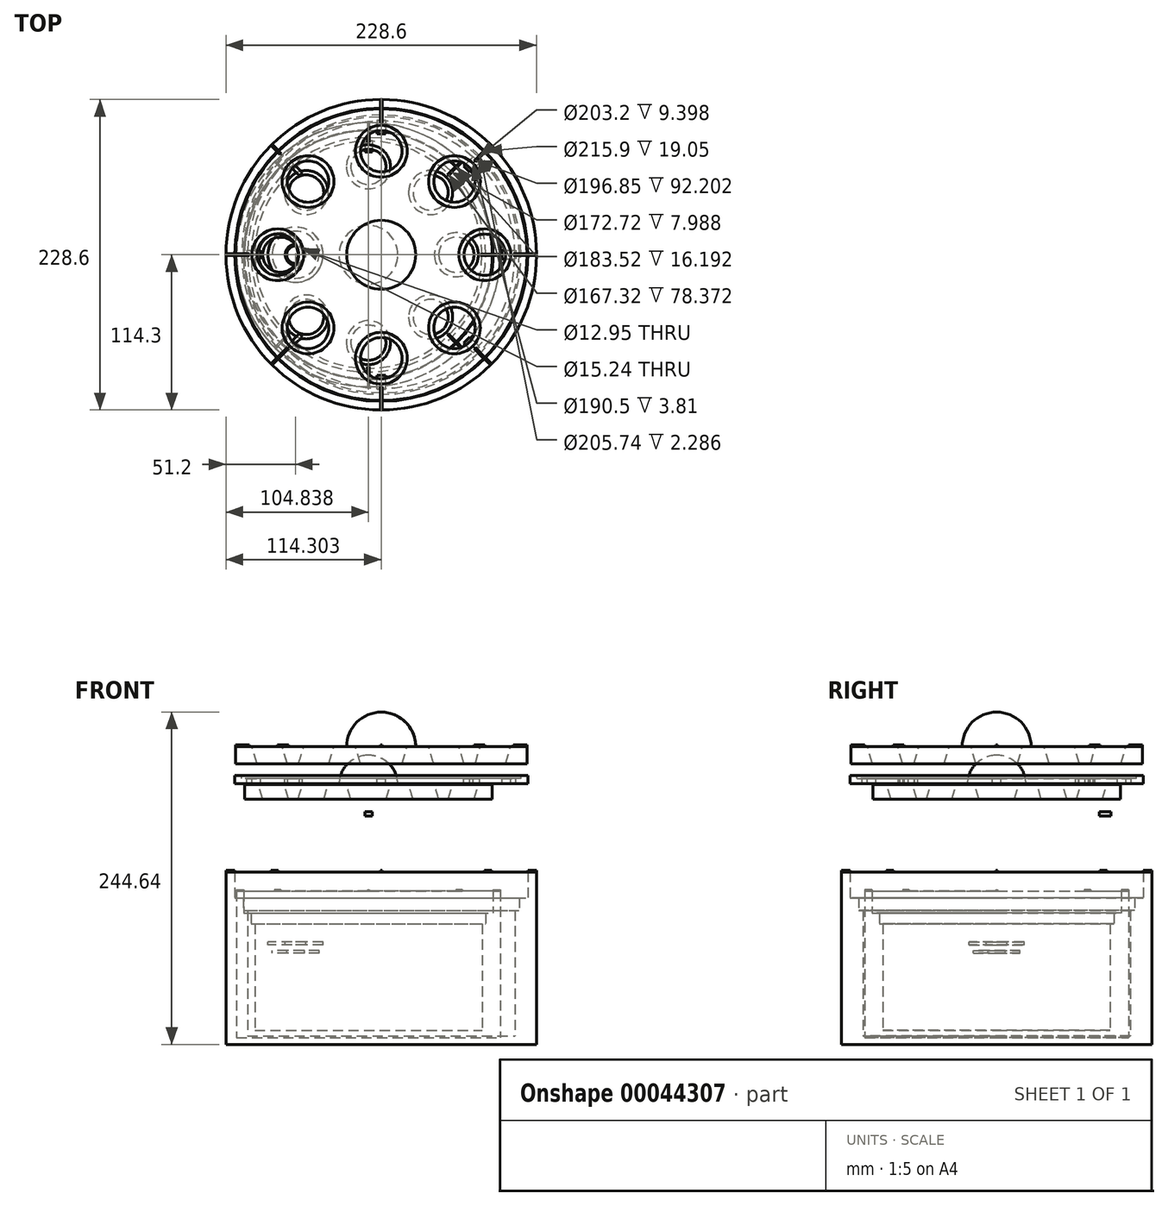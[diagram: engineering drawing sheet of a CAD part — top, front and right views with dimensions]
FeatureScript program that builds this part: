
annotation { "Feature Type Name" : "Feature", "Feature Type Description" : "" }
export const myFeature = defineFeature(function(context is Context, id is Id, definition is map)
    precondition{}
    {
        {
            var Q0;
            Q0=qCreatedBy(makeId("Front.planeOp"),FACE);
            var sketch = newSketch(context, id + "F0", { "sketchPlane" : qUnion([Q0])});
            skLineSegment(sketch, "E0", {"start": v(69.45, 56.08) * mm, "end": v(69.45, 18.25) * mm});
            skLineSegment(sketch, "E1", {"start": v(63.1, 57.26) * mm, "end": v(63.1, 18.31) * mm});
            skSolve(sketch);
        }
        {
            var Q0;
            Q0=qCreatedBy(makeId("Front.planeOp"),FACE);
            var sketch = newSketch(context, id + "F1", { "sketchPlane" : qUnion([Q0])});
            skLineSegment(sketch, "E2.bottom", {"start": v(-44.21, 186.24) * mm, "end": v(63.1, 186.24) * mm});
            skLineSegment(sketch, "E2.top", {"start": v(-44.21, 173.54) * mm, "end": v(63.1, 173.54) * mm});
            skLineSegment(sketch, "E2.left", {"start": v(-44.21, 186.24) * mm, "end": v(-44.21, 173.54) * mm});
            skLineSegment(sketch, "E2.right", {"start": v(63.1, 186.24) * mm, "end": v(63.1, 173.54) * mm});
            skLineSegment(sketch, "E3", {"start": v(63.1, 186.24) * mm, "end": v(63.1, 211.64) * mm});
            skArc(sketch, "E4", {"start": v(63.1, 211.64) * mm, "mid": v(45.14, 204.2) * mm, "end": v(37.7, 186.24) * mm});
            skSolve(sketch);
        }
        {
            var Q0;
            Q0=makeQuery(id+"F1.imprint","IMPRINT",FACE,{"disambiguationData":[TD([[makeQuery(id+"F1.imprint","IMPRINT",EDGE,{"derivedFrom":sQuery(id+"F1.wireOp",EDGE,"E2.bottom")}),-1.0]])]});
            var Q1;
            {var subQ1=sQuery(id+"F1.wireOp",EDGE,"E3");Q1=makeQuery(id+"F1.imprint","IMPRINT",FACE,{"disambiguationData":[TD([[makeQuery(id+"F1.imprint","IMPRINT",EDGE,{"derivedFrom":subQ1}),1.0]])]});}
            var Q2;
            Q2=sQuery(id+"F1.wireOp",EDGE,"E2.right");
            revolve(context, id + "F2", {"entities" : qUnion([Q0, Q1]), "axis" : qUnion([Q2]), "revolveType" : RevolveType.FULL});
        }
        {
            var Q0;
            Q0=qCreatedBy(makeId("Front.planeOp"),FACE);
            var sketch = newSketch(context, id + "F3", { "sketchPlane" : qUnion([Q0])});
            skLineSegment(sketch, "E5", {"start": v(-51.2, 94) * mm, "end": v(-51.2, -33) * mm});
            skLineSegment(sketch, "E6", {"start": v(-51.2, -33) * mm, "end": v(63.1, -33) * mm});
            skLineSegment(sketch, "E7", {"start": v(63.1, -33) * mm, "end": v(63.1, -26.65) * mm});
            skLineSegment(sketch, "E8", {"start": v(63.1, -26.65) * mm, "end": v(-38.5, -26.65) * mm});
            skLineSegment(sketch, "E9", {"start": v(-38.5, -26.65) * mm, "end": v(-38.5, 74.95) * mm});
            skLineSegment(sketch, "E10", {"start": v(-38.5, 74.95) * mm, "end": v(-44.85, 74.95) * mm});
            skLineSegment(sketch, "E11", {"start": v(-44.85, 74.95) * mm, "end": v(-44.85, 94) * mm});
            skLineSegment(sketch, "E12", {"start": v(-44.85, 94) * mm, "end": v(-51.2, 94) * mm});
            skLineSegment(sketch, "E13", {"start": v(-38.5, 65.56) * mm, "end": v(-35.32, 65.56) * mm});
            skLineSegment(sketch, "E14", {"start": v(-35.32, 65.56) * mm, "end": v(-35.32, -26.65) * mm});
            skSolve(sketch);
        }
        {
            var Q0;
            Q0=makeQuery(id+"F3.imprint","IMPRINT",FACE,{"disambiguationData":[TD([[makeQuery(id+"F3.imprint","IMPRINT",EDGE,{"derivedFrom":sQuery(id+"F3.wireOp",EDGE,"E5")}),1.0]])]});
            var Q1;
            {var subQ4=sQuery(id+"F3.wireOp",EDGE,"E13");Q1=makeQuery(id+"F3.imprint","IMPRINT",FACE,{"disambiguationData":[TD([[makeQuery(id+"F3.imprint","IMPRINT",EDGE,{"derivedFrom":subQ4}),-1.0]])]});}
            var Q2;
            Q2=sQuery(id+"F3.wireOp",EDGE,"E7");
            revolve(context, id + "F4", {"entities" : qUnion([Q0, Q1]), "axis" : qUnion([Q2]), "revolveType" : RevolveType.FULL});
        }
        {
            var Q0;
            Q0=qCreatedBy(makeId("Front.planeOp"),FACE);
            var sketch = newSketch(context, id + "F5", { "sketchPlane" : qUnion([Q0])});
            skLineSegment(sketch, "E15.top", {"start": v(-44.85, 159.05) * mm, "end": v(-32.15, 159.05) * mm});
            skLineSegment(sketch, "E15.left", {"start": v(-44.85, 162.6) * mm, "end": v(-44.85, 159.05) * mm});
            skLineSegment(sketch, "E15.right", {"start": v(-32.15, 162.86) * mm, "end": v(-32.15, 159.05) * mm});
            skLineSegment(sketch, "E16", {"start": v(-44.85, 162.6) * mm, "end": v(-44.85, 165.14) * mm});
            skLineSegment(sketch, "E17", {"start": v(-44.85, 165.14) * mm, "end": v(-39.77, 165.14) * mm});
            skLineSegment(sketch, "E18", {"start": v(-39.77, 165.14) * mm, "end": v(-39.77, 162.86) * mm});
            skLineSegment(sketch, "E19", {"start": v(-39.77, 162.86) * mm, "end": v(-32.15, 162.86) * mm});
            skLineSegment(sketch, "E20", {"start": v(63.1, 167.98) * mm, "end": v(63.1, 134.88) * mm});
            skSolve(sketch);
        }
        {
            var Q0;
            Q0=makeQuery(id+"F5.imprint","IMPRINT",FACE,{"disambiguationData":[TD([[makeQuery(id+"F5.imprint","IMPRINT",EDGE,{"derivedFrom":sQuery(id+"F5.wireOp",EDGE,"E15.top")}),1.0]])]});
            var Q1;
            Q1=sQuery(id+"F1.wireOp",EDGE,"E2.right");
            revolve(context, id + "F6", {"entities" : qUnion([Q0]), "axis" : qUnion([Q1]), "revolveType" : RevolveType.FULL});
        }
        {
            var Q0;
            Q0=qCreatedBy(makeId("Front.planeOp"),FACE);
            var sketch = newSketch(context, id + "F7", { "sketchPlane" : qUnion([Q0])});
            skLineSegment(sketch, "E21", {"start": v(-32.15, 186.24) * mm, "end": v(-13.1, 186.24) * mm});
            skLineSegment(sketch, "E22", {"start": v(-13.1, 186.24) * mm, "end": v(-13.1, 173.54) * mm});
            skLineSegment(sketch, "E23", {"start": v(-13.1, 173.54) * mm, "end": v(-28.34, 173.54) * mm});
            skLineSegment(sketch, "E24", {"start": v(-28.34, 173.54) * mm, "end": v(-32.15, 186.24) * mm});
            skSolve(sketch);
        }
        {
            var Q0;
            Q0 = qSketchRegion(id + "F7", true);
            var Q1;
            Q1=sQuery(id+"F7.wireOp",EDGE,"E22");
            revolve(context, id + "F8", {"entities" : qUnion([Q0]), "axis" : qUnion([Q1]), "revolveType" : RevolveType.FULL});
        }
        {
            var Q0;
            Q0=makeQuery(id+"F8.opRevolve","SWEPT_BODY",BODY,{"disambiguationData":[OSD([sQuery(id+"F7.wireOp",EDGE,"E21"),sQuery(id+"F7.wireOp",EDGE,"E22"),sQuery(id+"F7.wireOp",EDGE,"E23"),sQuery(id+"F7.wireOp",EDGE,"E24")])]});
            var Q1;
            Q1=makeQuery(id+"F2.opRevolve","SWEPT_BODY",BODY,{"disambiguationData":[OSD([sQuery(id+"F1.wireOp",EDGE,"E2.bottom"),sQuery(id+"F1.wireOp",EDGE,"E2.top"),sQuery(id+"F1.wireOp",EDGE,"E2.left"),sQuery(id+"F1.wireOp",EDGE,"E2.right")])]});
            booleanBodies(context, id + "F9", {"operationType" : BooleanOperationType.SUBTRACTION, "tools" : qUnion([Q0]), "targets" : qUnion([Q1])});
        }
        {
            var Q0;
            Q0=qCreatedBy(makeId("Front.planeOp"),FACE);
            var sketch = newSketch(context, id + "F10", { "sketchPlane" : qUnion([Q0])});
            skLineSegment(sketch, "E25", {"start": v(139.3, 186.24) * mm, "end": v(158.35, 186.24) * mm});
            skLineSegment(sketch, "E26", {"start": v(158.35, 186.24) * mm, "end": v(154.54, 173.54) * mm});
            skLineSegment(sketch, "E27", {"start": v(154.54, 173.54) * mm, "end": v(139.3, 173.54) * mm});
            skLineSegment(sketch, "E28", {"start": v(139.3, 173.54) * mm, "end": v(139.3, 186.24) * mm});
            skSolve(sketch);
        }
        {
            var Q0;
            Q0=makeQuery(id+"F10.imprint","IMPRINT",FACE,{"disambiguationData":[TD([[makeQuery(id+"F10.imprint","IMPRINT",EDGE,{"derivedFrom":sQuery(id+"F10.wireOp",EDGE,"E25")}),-1.0]])]});
            var Q1;
            Q1=sQuery(id+"F10.wireOp",EDGE,"E28");
            revolve(context, id + "F11", {"entities" : qUnion([Q0]), "axis" : qUnion([Q1]), "revolveType" : RevolveType.FULL});
        }
        {
            var Q0;
            Q0=makeQuery(id+"F11.opRevolve","SWEPT_BODY",BODY,{"disambiguationData":[OSD([sQuery(id+"F10.wireOp",EDGE,"E25"),sQuery(id+"F10.wireOp",EDGE,"E26"),sQuery(id+"F10.wireOp",EDGE,"E27"),sQuery(id+"F10.wireOp",EDGE,"E28")])]});
            var Q1;
            Q1=makeQuery(id+"F2.opRevolve","SWEPT_BODY",BODY,{"disambiguationData":[OSD([sQuery(id+"F1.wireOp",EDGE,"E2.bottom"),sQuery(id+"F1.wireOp",EDGE,"E2.top"),sQuery(id+"F1.wireOp",EDGE,"E2.left"),sQuery(id+"F1.wireOp",EDGE,"E2.right")])]});
            booleanBodies(context, id + "F12", {"operationType" : BooleanOperationType.SUBTRACTION, "tools" : qUnion([Q0]), "targets" : qUnion([Q1])});
        }
        {
            var Q0;
            Q0=qCreatedBy(makeId("Top.planeOp"),FACE);
            var sketch = newSketch(context, id + "F13", { "sketchPlane" : qUnion([Q0])});
            skLineSegment(sketch, "E29", {"start": v(-63.2, 76.2) * mm, "end": v(69.43, 76.2) * mm});
            skSolve(sketch);
        }
        {
            var Q0;
            Q0=sQuery(id+"F13.wireOp",EDGE,"E29");
            var Q1;
            Q1 = qConstructionFilter(qBodyType(qCreatedBy(id + "F18" ,EDGE), BodyType.WIRE), ConstructionObject.NO);
            extrude(context, id + "F14", {"bodyType" : ToolBodyType.SURFACE, "surfaceEntities" : qUnion([Q0, Q1]), "depth" : 76.2 * mm});
        }
        {
            var Q0;
            Q0=makeQuery(id+"F14.opExtrude","SWEPT_FACE",FACE,{"disambiguationData":[OSD([sQuery(id+"F13.wireOp",EDGE,"E29")])]});
            var sketch = newSketch(context, id + "F15", { "sketchPlane" : qUnion([Q0])});
            skLineSegment(sketch, "E30", {"start": v(63.1, 186.24) * mm, "end": v(82.15, 186.24) * mm});
            skLineSegment(sketch, "E31", {"start": v(82.15, 186.24) * mm, "end": v(78.34, 173.54) * mm});
            skLineSegment(sketch, "E32", {"start": v(78.34, 173.54) * mm, "end": v(63.1, 173.54) * mm});
            skLineSegment(sketch, "E33", {"start": v(63.1, 173.54) * mm, "end": v(63.1, 186.24) * mm});
            skSolve(sketch);
        }
        {
            var Q0;
            Q0 = qSketchRegion(id + "F15", true);
            var Q1;
            Q1=sQuery(id+"F15.wireOp",EDGE,"E33");
            revolve(context, id + "F16", {"entities" : qUnion([Q0]), "axis" : qUnion([Q1]), "revolveType" : RevolveType.FULL});
        }
        {
            var Q0;
            Q0=makeQuery(id+"F16.opRevolve","SWEPT_BODY",BODY,{"disambiguationData":[OSD([sQuery(id+"F15.wireOp",EDGE,"E30"),sQuery(id+"F15.wireOp",EDGE,"E31"),sQuery(id+"F15.wireOp",EDGE,"E32"),sQuery(id+"F15.wireOp",EDGE,"E33")])]});
            var Q1;
            Q1=makeQuery(id+"F2.opRevolve","SWEPT_BODY",BODY,{"disambiguationData":[OSD([sQuery(id+"F1.wireOp",EDGE,"E2.bottom"),sQuery(id+"F1.wireOp",EDGE,"E2.top"),sQuery(id+"F1.wireOp",EDGE,"E2.left"),sQuery(id+"F1.wireOp",EDGE,"E2.right")])]});
            booleanBodies(context, id + "F17", {"operationType" : BooleanOperationType.SUBTRACTION, "tools" : qUnion([Q0]), "targets" : qUnion([Q1])});
        }
        {
            var Q0;
            Q0=qCreatedBy(makeId("Top.planeOp"),FACE);
            var sketch = newSketch(context, id + "F18", { "sketchPlane" : qUnion([Q0])});
            skLineSegment(sketch, "E34", {"start": v(-48.86, -76.2) * mm, "end": v(52.96, -76.2) * mm});
            skSolve(sketch);
        }
        {
            var Q0;
            Q0 = qSketchRegion(id + "F18", true);
            var Q1;
            Q1=sQuery(id+"F18.wireOp",EDGE,"E34");
            extrude(context, id + "F19", {"entities" : qUnion([Q0]), "bodyType" : ToolBodyType.SURFACE, "surfaceEntities" : qUnion([Q1]), "depth" : 76.2 * mm});
        }
        {
            var Q0;
            Q0=makeQuery(id+"F19.opExtrude","SWEPT_FACE",FACE,{"disambiguationData":[OSD([sQuery(id+"F18.wireOp",EDGE,"E34")])]});
            var sketch = newSketch(context, id + "F20", { "sketchPlane" : qUnion([Q0])});
            skLineSegment(sketch, "E35", {"start": v(63.1, 186.24) * mm, "end": v(44.05, 186.24) * mm});
            skLineSegment(sketch, "E36", {"start": v(44.05, 186.24) * mm, "end": v(47.86, 173.54) * mm});
            skLineSegment(sketch, "E37", {"start": v(47.86, 173.54) * mm, "end": v(63.1, 173.54) * mm});
            skLineSegment(sketch, "E38", {"start": v(63.1, 173.54) * mm, "end": v(63.1, 186.24) * mm});
            skSolve(sketch);
        }
        {
            var Q0;
            Q0 = qSketchRegion(id + "F20", true);
            var Q1;
            Q1=sQuery(id+"F20.wireOp",EDGE,"E38");
            revolve(context, id + "F21", {"entities" : qUnion([Q0]), "axis" : qUnion([Q1]), "revolveType" : RevolveType.FULL});
        }
        {
            var Q0;
            Q0=makeQuery(id+"F21.opRevolve","SWEPT_BODY",BODY,{"disambiguationData":[OSD([sQuery(id+"F20.wireOp",EDGE,"E35"),sQuery(id+"F20.wireOp",EDGE,"E36"),sQuery(id+"F20.wireOp",EDGE,"E37"),sQuery(id+"F20.wireOp",EDGE,"E38")])]});
            var Q1;
            Q1=makeQuery(id+"F2.opRevolve","SWEPT_BODY",BODY,{"disambiguationData":[OSD([sQuery(id+"F1.wireOp",EDGE,"E2.bottom"),sQuery(id+"F1.wireOp",EDGE,"E2.top"),sQuery(id+"F1.wireOp",EDGE,"E2.left"),sQuery(id+"F1.wireOp",EDGE,"E2.right")])]});
            booleanBodies(context, id + "F22", {"operationType" : BooleanOperationType.SUBTRACTION, "tools" : qUnion([Q0]), "targets" : qUnion([Q1])});
        }
        {
            var Q0;
            Q0=makeQuery(id+"F6.opRevolve","SWEPT_FACE",FACE,{"disambiguationData":[OSD([sQuery(id+"F5.wireOp",EDGE,"E19")])]});
            var sketch = newSketch(context, id + "F23", { "sketchPlane" : qUnion([Q0])});
            skLineSegment(sketch, "E39", {"start": v(63.1, 76.2) * mm, "end": v(-13.1, 0) * mm});
            skLineSegment(sketch, "E40", {"start": v(-13.1, 0) * mm, "end": v(63.1, -76.2) * mm});
            skLineSegment(sketch, "E41", {"start": v(63.1, -76.2) * mm, "end": v(139.3, 0) * mm});
            skLineSegment(sketch, "E42", {"start": v(139.3, 0) * mm, "end": v(63.1, 76.2) * mm});
            skLineSegment(sketch, "E43", {"start": v(25, -38.1) * mm, "end": v(101.2, 38.1) * mm});
            skLineSegment(sketch, "E44", {"start": v(101.2, -38.1) * mm, "end": v(25, 38.1) * mm});
            skLineSegment(sketch, "E45", {"start": v(63.1, 76.2) * mm, "end": v(63.1, -76.2) * mm});
            skLineSegment(sketch, "E46", {"start": v(-13.1, 0) * mm, "end": v(139.3, 0) * mm});
            skLineSegment(sketch, "E47", {"start": v(63.1, 0) * mm, "end": v(63.1, 88.9) * mm});
            skLineSegment(sketch, "E48", {"start": v(63.1, 0) * mm, "end": v(125.96, 62.86) * mm});
            skLineSegment(sketch, "E49", {"start": v(63.1, 0) * mm, "end": v(152, 0) * mm});
            skLineSegment(sketch, "E50", {"start": v(63.1, 0) * mm, "end": v(125.96, -62.86) * mm});
            skLineSegment(sketch, "E51", {"start": v(63.1, 0) * mm, "end": v(63.1, -88.9) * mm});
            skLineSegment(sketch, "E52", {"start": v(63.1, 0) * mm, "end": v(3.83, -59.27) * mm});
            skLineSegment(sketch, "E53", {"start": v(63.1, 0) * mm, "end": v(-25.8, 0) * mm});
            skLineSegment(sketch, "E54", {"start": v(63.1, 0) * mm, "end": v(3.83, 59.27) * mm});
            skSolve(sketch);
        }
        {
            var Q0;
            Q0=sQuery(id+"F23.wireOp",EDGE,"E44");
            extrude(context, id + "F24", {"bodyType" : ToolBodyType.SURFACE, "surfaceEntities" : qUnion([Q0]), "depth" : 76.2 * mm});
        }
        {
            var Q0;
            Q0=sQuery(id+"F23.wireOp",EDGE,"E43");
            extrude(context, id + "F25", {"bodyType" : ToolBodyType.SURFACE, "surfaceEntities" : qUnion([Q0]), "depth" : 76.2 * mm});
        }
        {
            var Q0;
            Q0=makeQuery(id+"F25.opExtrude","SWEPT_FACE",FACE,{"disambiguationData":[OSD([sQuery(id+"F23.wireOp",EDGE,"E43")])]});
            var sketch = newSketch(context, id + "F26", { "sketchPlane" : qUnion([Q0])});
            skLineSegment(sketch, "E55", {"start": v(101.77, 186.24) * mm, "end": v(120.82, 186.24) * mm});
            skLineSegment(sketch, "E56", {"start": v(101.77, 186.24) * mm, "end": v(105.58, 173.54) * mm});
            skLineSegment(sketch, "E57", {"start": v(120.82, 173.54) * mm, "end": v(105.58, 173.54) * mm});
            skLineSegment(sketch, "E58", {"start": v(120.82, 173.54) * mm, "end": v(120.82, 186.24) * mm});
            skSolve(sketch);
        }
        {
            var Q0;
            Q0=makeQuery(id+"F26.imprint","IMPRINT",FACE,{"disambiguationData":[TD([[makeQuery(id+"F26.imprint","IMPRINT",EDGE,{"derivedFrom":sQuery(id+"F26.wireOp",EDGE,"E55")}),-1.0]])]});
            var Q1;
            Q1=sQuery(id+"F26.wireOp",EDGE,"E58");
            revolve(context, id + "F27", {"entities" : qUnion([Q0]), "axis" : qUnion([Q1]), "revolveType" : RevolveType.FULL});
        }
        {
            var Q0;
            Q0=makeQuery(id+"F27.opRevolve","SWEPT_BODY",BODY,{"disambiguationData":[OSD([sQuery(id+"F26.wireOp",EDGE,"E55"),sQuery(id+"F26.wireOp",EDGE,"E56"),sQuery(id+"F26.wireOp",EDGE,"E57"),sQuery(id+"F26.wireOp",EDGE,"E58")])]});
            var Q1;
            Q1=makeQuery(id+"F2.opRevolve","SWEPT_BODY",BODY,{"disambiguationData":[OSD([sQuery(id+"F1.wireOp",EDGE,"E2.bottom"),sQuery(id+"F1.wireOp",EDGE,"E2.top"),sQuery(id+"F1.wireOp",EDGE,"E2.left"),sQuery(id+"F1.wireOp",EDGE,"E2.right")])]});
            booleanBodies(context, id + "F28", {"operationType" : BooleanOperationType.SUBTRACTION, "tools" : qUnion([Q0]), "targets" : qUnion([Q1])});
        }
        {
            var Q0;
            Q0=makeQuery(id+"F26.imprint","IMPRINT",FACE,{"disambiguationData":[TD([[makeQuery(id+"F26.imprint","IMPRINT",EDGE,{"derivedFrom":makeQuery(id+"F25.opExtrude","SWEPT_EDGE",EDGE,{"disambiguationData":[OSD([sQuery(id+"F23.wireOp",VERTEX,"E43.start")])]})}),-1.0]])]});
            var sketch = newSketch(context, id + "F29", { "sketchPlane" : qUnion([Q0])});
            skLineSegment(sketch, "E59", {"start": v(-31.58, 186.24) * mm, "end": v(-50.63, 186.24) * mm});
            skLineSegment(sketch, "E60", {"start": v(-50.63, 186.24) * mm, "end": v(-46.82, 173.54) * mm});
            skLineSegment(sketch, "E61", {"start": v(-46.82, 173.54) * mm, "end": v(-31.58, 173.54) * mm});
            skLineSegment(sketch, "E62", {"start": v(-31.58, 173.54) * mm, "end": v(-31.58, 186.24) * mm});
            skSolve(sketch);
        }
        {
            var Q0;
            Q0=makeQuery(id+"F29.imprint","IMPRINT",FACE,{"disambiguationData":[TD([[makeQuery(id+"F29.imprint","IMPRINT",EDGE,{"derivedFrom":sQuery(id+"F29.wireOp",EDGE,"E59")}),1.0]])]});
            var Q1;
            Q1=sQuery(id+"F29.wireOp",EDGE,"E62");
            revolve(context, id + "F30", {"entities" : qUnion([Q0]), "axis" : qUnion([Q1]), "revolveType" : RevolveType.FULL});
        }
        {
            var Q0;
            Q0=makeQuery(id+"F30.opRevolve","SWEPT_BODY",BODY,{"disambiguationData":[OSD([sQuery(id+"F29.wireOp",EDGE,"E59"),sQuery(id+"F29.wireOp",EDGE,"E60"),sQuery(id+"F29.wireOp",EDGE,"E61"),sQuery(id+"F29.wireOp",EDGE,"E62")])]});
            var Q1;
            Q1=makeQuery(id+"F2.opRevolve","SWEPT_BODY",BODY,{"disambiguationData":[OSD([sQuery(id+"F1.wireOp",EDGE,"E2.bottom"),sQuery(id+"F1.wireOp",EDGE,"E2.top"),sQuery(id+"F1.wireOp",EDGE,"E2.left"),sQuery(id+"F1.wireOp",EDGE,"E2.right")])]});
            booleanBodies(context, id + "F31", {"operationType" : BooleanOperationType.SUBTRACTION, "tools" : qUnion([Q0]), "targets" : qUnion([Q1])});
        }
        {
            var Q0;
            Q0=makeQuery(id+"F24.opExtrude","SWEPT_FACE",FACE,{"disambiguationData":[OSD([sQuery(id+"F23.wireOp",EDGE,"E44")])]});
            var sketch = newSketch(context, id + "F32", { "sketchPlane" : qUnion([Q0])});
            skLineSegment(sketch, "E63", {"start": v(-120.82, 186.24) * mm, "end": v(-139.87, 186.24) * mm});
            skLineSegment(sketch, "E64", {"start": v(-139.87, 186.24) * mm, "end": v(-136.06, 173.54) * mm});
            skLineSegment(sketch, "E65", {"start": v(-136.06, 173.54) * mm, "end": v(-120.82, 173.54) * mm});
            skLineSegment(sketch, "E66", {"start": v(-120.82, 173.54) * mm, "end": v(-120.82, 186.24) * mm});
            skSolve(sketch);
        }
        {
            var Q0;
            Q0=makeQuery(id+"F32.imprint","IMPRINT",FACE,{"disambiguationData":[TD([[makeQuery(id+"F32.imprint","IMPRINT",EDGE,{"derivedFrom":sQuery(id+"F32.wireOp",EDGE,"E63")}),1.0]])]});
            var Q1;
            Q1=sQuery(id+"F32.wireOp",EDGE,"E66");
            revolve(context, id + "F33", {"entities" : qUnion([Q0]), "axis" : qUnion([Q1]), "revolveType" : RevolveType.FULL});
        }
        {
            var Q0;
            Q0=makeQuery(id+"F33.opRevolve","SWEPT_BODY",BODY,{"disambiguationData":[OSD([sQuery(id+"F32.wireOp",EDGE,"E63"),sQuery(id+"F32.wireOp",EDGE,"E64"),sQuery(id+"F32.wireOp",EDGE,"E65"),sQuery(id+"F32.wireOp",EDGE,"E66")])]});
            var Q1;
            Q1=makeQuery(id+"F2.opRevolve","SWEPT_BODY",BODY,{"disambiguationData":[OSD([sQuery(id+"F1.wireOp",EDGE,"E2.bottom"),sQuery(id+"F1.wireOp",EDGE,"E2.top"),sQuery(id+"F1.wireOp",EDGE,"E2.left"),sQuery(id+"F1.wireOp",EDGE,"E2.right")])]});
            booleanBodies(context, id + "F34", {"operationType" : BooleanOperationType.SUBTRACTION, "tools" : qUnion([Q0]), "targets" : qUnion([Q1])});
        }
        {
            var Q0;
            Q0=makeQuery(id+"F24.opExtrude","SWEPT_FACE",FACE,{"disambiguationData":[OSD([sQuery(id+"F23.wireOp",EDGE,"E44")])]});
            var sketch = newSketch(context, id + "F35", { "sketchPlane" : qUnion([Q0])});
            skLineSegment(sketch, "E67", {"start": v(50.63, 186.24) * mm, "end": v(31.58, 186.24) * mm});
            skLineSegment(sketch, "E68", {"start": v(31.58, 186.24) * mm, "end": v(31.58, 173.54) * mm});
            skLineSegment(sketch, "E69", {"start": v(31.58, 173.54) * mm, "end": v(46.82, 173.54) * mm});
            skLineSegment(sketch, "E70", {"start": v(46.82, 173.54) * mm, "end": v(50.63, 186.24) * mm});
            skSolve(sketch);
        }
        {
            var Q0;
            Q0=makeQuery(id+"F35.imprint","IMPRINT",FACE,{"disambiguationData":[TD([[makeQuery(id+"F35.imprint","IMPRINT",EDGE,{"derivedFrom":sQuery(id+"F35.wireOp",EDGE,"E67")}),1.0]])]});
            var Q1;
            Q1=sQuery(id+"F35.wireOp",EDGE,"E68");
            revolve(context, id + "F36", {"entities" : qUnion([Q0]), "axis" : qUnion([Q1]), "revolveType" : RevolveType.FULL});
        }
        {
            var Q0;
            Q0=makeQuery(id+"F36.opRevolve","SWEPT_BODY",BODY,{"disambiguationData":[OSD([sQuery(id+"F35.wireOp",EDGE,"E67"),sQuery(id+"F35.wireOp",EDGE,"E68"),sQuery(id+"F35.wireOp",EDGE,"E69"),sQuery(id+"F35.wireOp",EDGE,"E70")])]});
            var Q1;
            Q1=makeQuery(id+"F2.opRevolve","SWEPT_BODY",BODY,{"disambiguationData":[OSD([sQuery(id+"F1.wireOp",EDGE,"E2.bottom"),sQuery(id+"F1.wireOp",EDGE,"E2.top"),sQuery(id+"F1.wireOp",EDGE,"E2.left"),sQuery(id+"F1.wireOp",EDGE,"E2.right")])]});
            booleanBodies(context, id + "F37", {"operationType" : BooleanOperationType.SUBTRACTION, "tools" : qUnion([Q0]), "targets" : qUnion([Q1])});
        }
        {
            var Q0;
            Q0=makeQuery(id+"F6.opRevolve","SWEPT_FACE",FACE,{"disambiguationData":[OSD([sQuery(id+"F5.wireOp",EDGE,"E19")])]});
            var sketch = newSketch(context, id + "F38", { "sketchPlane" : qUnion([Q0])});
            skLineSegment(sketch, "E71.bottom", {"start": v(59.93, 99.06) * mm, "end": v(66.28, 99.06) * mm});
            skLineSegment(sketch, "E71.top", {"start": v(59.93, 88.9) * mm, "end": v(66.28, 88.9) * mm});
            skLineSegment(sketch, "E71.left", {"start": v(59.93, 99.06) * mm, "end": v(59.93, 88.9) * mm});
            skLineSegment(sketch, "E71.right", {"start": v(66.28, 99.06) * mm, "end": v(66.28, 88.9) * mm});
            skLineSegment(sketch, "E72.bottom", {"start": v(123.72, -65.1) * mm, "end": v(128.2, -60.62) * mm});
            skLineSegment(sketch, "E72.top", {"start": v(130.9, -72.3) * mm, "end": v(135.4, -67.8) * mm});
            skLineSegment(sketch, "E72.left", {"start": v(123.72, -65.1) * mm, "end": v(130.9, -72.3) * mm});
            skLineSegment(sketch, "E72.right", {"start": v(128.2, -60.62) * mm, "end": v(135.4, -67.8) * mm});
            skLineSegment(sketch, "E73.bottom", {"start": v(-35.96, 3.18) * mm, "end": v(-25.8, 3.18) * mm});
            skLineSegment(sketch, "E73.top", {"start": v(-35.96, -3.18) * mm, "end": v(-25.8, -3.18) * mm});
            skLineSegment(sketch, "E73.left", {"start": v(-35.96, 3.18) * mm, "end": v(-35.96, -3.18) * mm});
            skLineSegment(sketch, "E73.right", {"start": v(-25.8, 3.18) * mm, "end": v(-25.8, -3.18) * mm});
            skLineSegment(sketch, "E74.bottom", {"start": v(152, 3.17) * mm, "end": v(162.16, 3.17) * mm});
            skLineSegment(sketch, "E74.top", {"start": v(152, -3.18) * mm, "end": v(162.16, -3.18) * mm});
            skLineSegment(sketch, "E74.left", {"start": v(152, 3.17) * mm, "end": v(152, -3.17) * mm});
            skLineSegment(sketch, "E74.right", {"start": v(162.16, 3.17) * mm, "end": v(162.16, -3.17) * mm});
            skLineSegment(sketch, "E75.bottom", {"start": v(123.72, 65.1) * mm, "end": v(130.9, 72.3) * mm});
            skLineSegment(sketch, "E75.top", {"start": v(128.2, 60.62) * mm, "end": v(135.4, 67.8) * mm});
            skLineSegment(sketch, "E75.left", {"start": v(123.72, 65.1) * mm, "end": v(128.2, 60.62) * mm});
            skLineSegment(sketch, "E75.right", {"start": v(130.9, 72.3) * mm, "end": v(135.4, 67.8) * mm});
            skLineSegment(sketch, "E76.bottom", {"start": v(59.93, -99.06) * mm, "end": v(59.93, -88.9) * mm});
            skLineSegment(sketch, "E76.top", {"start": v(66.28, -99.06) * mm, "end": v(66.28, -88.9) * mm});
            skLineSegment(sketch, "E76.left", {"start": v(59.93, -99.06) * mm, "end": v(66.28, -99.06) * mm});
            skLineSegment(sketch, "E76.right", {"start": v(59.93, -88.9) * mm, "end": v(66.28, -88.9) * mm});
            skLineSegment(sketch, "E77.bottom", {"start": v(-8.07, 68.92) * mm, "end": v(-5.82, 71.17) * mm});
            skLineSegment(sketch, "E77.top", {"start": v(2.71, 58.15) * mm, "end": v(4.96, 60.4) * mm});
            skLineSegment(sketch, "E77.left", {"start": v(-8.07, 68.92) * mm, "end": v(2.71, 58.15) * mm});
            skLineSegment(sketch, "E77.right", {"start": v(-5.82, 71.17) * mm, "end": v(4.96, 60.4) * mm});
            skLineSegment(sketch, "E78.bottom", {"start": v(2.71, -58.15) * mm, "end": v(4.96, -60.4) * mm});
            skLineSegment(sketch, "E78.top", {"start": v(-8.07, -68.92) * mm, "end": v(-5.82, -71.17) * mm});
            skLineSegment(sketch, "E78.left", {"start": v(2.71, -58.15) * mm, "end": v(-8.07, -68.92) * mm});
            skLineSegment(sketch, "E78.right", {"start": v(4.96, -60.4) * mm, "end": v(-5.82, -71.17) * mm});
            skSolve(sketch);
        }
        {
            var Q0;
            {var subQ5=sQuery(id+"F38.wireOp",EDGE,"E71.top");Q0=makeQuery(id+"F38.imprint","IMPRINT",FACE,{"disambiguationData":[TD([[makeQuery(id+"F38.imprint","IMPRINT",EDGE,{"derivedFrom":subQ5}),1.0]])]});}
            var Q1;
            {var subQ5=sQuery(id+"F38.wireOp",EDGE,"E71.bottom");Q1=makeQuery(id+"F38.imprint","IMPRINT",FACE,{"disambiguationData":[TD([[makeQuery(id+"F38.imprint","IMPRINT",EDGE,{"derivedFrom":subQ5}),-1.0]])]});}
            var Q2;
            Q2=makeQuery(id+"F6.opRevolve","SWEPT_FACE",FACE,{"disambiguationData":[OSD([sQuery(id+"F5.wireOp",EDGE,"E15.top")])]});
            extrude(context, id + "F39", {"entities" : qUnion([Q0, Q1]), "endBound" : BoundingType.UP_TO_SURFACE, "oppositeDirection" : true, "endBoundEntityFace" : qUnion([Q2]), "depth" : 6.35 * mm});
        }
        {
            var Q0;
            {var subQ5=sQuery(id+"F38.wireOp",EDGE,"E75.right");Q0=makeQuery(id+"F38.imprint","IMPRINT",FACE,{"disambiguationData":[TD([[makeQuery(id+"F38.imprint","IMPRINT",EDGE,{"derivedFrom":subQ5}),-1.0]])]});}
            var Q1;
            {var subQ5=sQuery(id+"F38.wireOp",EDGE,"E75.left");Q1=makeQuery(id+"F38.imprint","IMPRINT",FACE,{"disambiguationData":[TD([[makeQuery(id+"F38.imprint","IMPRINT",EDGE,{"derivedFrom":subQ5}),1.0]])]});}
            var Q2;
            {var subQ5=sQuery(id+"F38.wireOp",EDGE,"E74.left");Q2=makeQuery(id+"F38.imprint","IMPRINT",FACE,{"disambiguationData":[TD([[makeQuery(id+"F38.imprint","IMPRINT",EDGE,{"derivedFrom":subQ5}),1.0]])]});}
            var Q3;
            {var subQ5=sQuery(id+"F38.wireOp",EDGE,"E74.right");Q3=makeQuery(id+"F38.imprint","IMPRINT",FACE,{"disambiguationData":[TD([[makeQuery(id+"F38.imprint","IMPRINT",EDGE,{"derivedFrom":subQ5}),-1.0]])]});}
            var Q4;
            {var subQ3=sQuery(id+"F38.wireOp",EDGE,"E72.bottom");Q4=makeQuery(id+"F38.imprint","IMPRINT",FACE,{"disambiguationData":[TD([[makeQuery(id+"F38.imprint","IMPRINT",EDGE,{"derivedFrom":subQ3}),-1.0]])]});}
            var Q5;
            {var subQ3=sQuery(id+"F38.wireOp",EDGE,"E72.top");Q5=makeQuery(id+"F38.imprint","IMPRINT",FACE,{"disambiguationData":[TD([[makeQuery(id+"F38.imprint","IMPRINT",EDGE,{"derivedFrom":subQ3}),1.0]])]});}
            var Q6;
            {var subQ0=sQuery(id+"F38.wireOp",EDGE,"E76.right");Q6=makeQuery(id+"F38.imprint","IMPRINT",FACE,{"disambiguationData":[TD([[makeQuery(id+"F38.imprint","IMPRINT",EDGE,{"derivedFrom":subQ0}),-1.0]])]});}
            var Q7;
            {var subQ5=sQuery(id+"F38.wireOp",EDGE,"E76.left");Q7=makeQuery(id+"F38.imprint","IMPRINT",FACE,{"disambiguationData":[TD([[makeQuery(id+"F38.imprint","IMPRINT",EDGE,{"derivedFrom":subQ5}),1.0]])]});}
            var Q8;
            {var subQ5=sQuery(id+"F38.wireOp",EDGE,"E78.bottom");Q8=makeQuery(id+"F38.imprint","IMPRINT",FACE,{"disambiguationData":[TD([[makeQuery(id+"F38.imprint","IMPRINT",EDGE,{"derivedFrom":subQ5}),-1.0]])]});}
            var Q9;
            {var subQ5=sQuery(id+"F38.wireOp",EDGE,"E78.top");Q9=makeQuery(id+"F38.imprint","IMPRINT",FACE,{"disambiguationData":[TD([[makeQuery(id+"F38.imprint","IMPRINT",EDGE,{"derivedFrom":subQ5}),1.0]])]});}
            var Q10;
            {var subQ5=sQuery(id+"F38.wireOp",EDGE,"E73.right");Q10=makeQuery(id+"F38.imprint","IMPRINT",FACE,{"disambiguationData":[TD([[makeQuery(id+"F38.imprint","IMPRINT",EDGE,{"derivedFrom":subQ5}),-1.0]])]});}
            var Q11;
            {var subQ5=sQuery(id+"F38.wireOp",EDGE,"E73.left");Q11=makeQuery(id+"F38.imprint","IMPRINT",FACE,{"disambiguationData":[TD([[makeQuery(id+"F38.imprint","IMPRINT",EDGE,{"derivedFrom":subQ5}),1.0]])]});}
            var Q12;
            {var subQ5=sQuery(id+"F38.wireOp",EDGE,"E77.top");Q12=makeQuery(id+"F38.imprint","IMPRINT",FACE,{"disambiguationData":[TD([[makeQuery(id+"F38.imprint","IMPRINT",EDGE,{"derivedFrom":subQ5}),1.0]])]});}
            var Q13;
            {var subQ5=sQuery(id+"F38.wireOp",EDGE,"E77.bottom");Q13=makeQuery(id+"F38.imprint","IMPRINT",FACE,{"disambiguationData":[TD([[makeQuery(id+"F38.imprint","IMPRINT",EDGE,{"derivedFrom":subQ5}),-1.0]])]});}
            var Q14;
            Q14=sQuery(id+"F38.wireOp",EDGE,"E75.top");
            var Q15;
            Q15=sQuery(id+"F38.wireOp",EDGE,"E75.bottom");
            var Q16;
            Q16=sQuery(id+"F38.wireOp",EDGE,"E75.right");
            var Q17;
            Q17=sQuery(id+"F38.wireOp",EDGE,"E75.left");
            var Q18;
            Q18=makeQuery(id+"F6.opRevolve","SWEPT_FACE",FACE,{"disambiguationData":[OSD([sQuery(id+"F5.wireOp",EDGE,"E15.top")])]});
            extrude(context, id + "F40", {"entities" : qUnion([Q0, Q1, Q2, Q3, Q4, Q5, Q6, Q7, Q8, Q9, Q10, Q11, Q12, Q13]), "surfaceEntities" : qUnion([Q14, Q15, Q16, Q17]), "endBound" : BoundingType.UP_TO_SURFACE, "oppositeDirection" : true, "endBoundEntityFace" : qUnion([Q18]), "depth" : 25.4 * mm});
        }
        {
            var Q0;
            Q0=makeQuery(id+"F2.opRevolve","SWEPT_FACE",FACE,{"disambiguationData":[OSD([sQuery(id+"F1.wireOp",EDGE,"E2.bottom")])]});
            var sketch = newSketch(context, id + "F41", { "sketchPlane" : qUnion([Q0])});
            skLineSegment(sketch, "E79", {"start": v(63.1, 76.2) * mm, "end": v(63.1, 107.32) * mm});
            skLineSegment(sketch, "E80", {"start": v(-13.1, 0) * mm, "end": v(-44.21, 0) * mm});
            skLineSegment(sketch, "E81", {"start": v(63.1, -76.2) * mm, "end": v(63.1, -107.32) * mm});
            skLineSegment(sketch, "E82", {"start": v(139.3, 0) * mm, "end": v(170.42, 0) * mm});
            skLineSegment(sketch, "E83", {"start": v(9.22, 53.88) * mm, "end": v(-12.78, 75.88) * mm});
            skLineSegment(sketch, "E84", {"start": v(116.98, 53.88) * mm, "end": v(138.99, 75.88) * mm});
            skLineSegment(sketch, "E85", {"start": v(116.98, -53.88) * mm, "end": v(138.99, -75.88) * mm});
            skLineSegment(sketch, "E86", {"start": v(9.22, -53.88) * mm, "end": v(-12.78, -75.88) * mm});
            skSolve(sketch);
        }
        {
            var Q0;
            {var subQ0=sQuery(id+"F1.wireOp",EDGE,"E2.bottom");Q0=makeQuery(id+"F41.imprint","IMPRINT",FACE,{"disambiguationData":[TD([[makeQuery(id+"F41.imprint","IMPRINT",EDGE,{"derivedFrom":makeQuery(id+"F2.opRevolve","SWEPT_EDGE",EDGE,{"disambiguationData":[OSD([subQ0,sQuery(id+"F1.wireOp",EDGE,"E4")])]})}),-1.0]])]});}
            var sketch = newSketch(context, id + "F42", { "sketchPlane" : qUnion([Q0])});
            skLineSegment(sketch, "E87.bottom", {"start": v(62.47, 107.32) * mm, "end": v(63.74, 107.32) * mm});
            skLineSegment(sketch, "E87.top", {"start": v(62.47, 97.16) * mm, "end": v(63.74, 97.16) * mm});
            skLineSegment(sketch, "E87.left", {"start": v(62.47, 107.32) * mm, "end": v(62.47, 97.16) * mm});
            skLineSegment(sketch, "E87.right", {"start": v(63.74, 107.32) * mm, "end": v(63.74, 97.16) * mm});
            skLineSegment(sketch, "E88.bottom", {"start": v(160.26, -0.63) * mm, "end": v(160.26, 0.63) * mm});
            skLineSegment(sketch, "E88.top", {"start": v(170.42, -0.63) * mm, "end": v(170.42, 0.63) * mm});
            skLineSegment(sketch, "E88.left", {"start": v(160.26, -0.64) * mm, "end": v(170.42, -0.64) * mm});
            skLineSegment(sketch, "E88.right", {"start": v(160.26, 0.64) * mm, "end": v(170.42, 0.64) * mm});
            skLineSegment(sketch, "E89.bottom", {"start": v(-34.05, 0.63) * mm, "end": v(-34.05, -0.63) * mm});
            skLineSegment(sketch, "E89.top", {"start": v(-44.21, 0.63) * mm, "end": v(-44.21, -0.63) * mm});
            skLineSegment(sketch, "E89.left", {"start": v(-34.05, 0.64) * mm, "end": v(-44.21, 0.64) * mm});
            skLineSegment(sketch, "E89.right", {"start": v(-34.05, -0.64) * mm, "end": v(-44.21, -0.64) * mm});
            skLineSegment(sketch, "E90.bottom", {"start": v(62.47, -97.16) * mm, "end": v(63.74, -97.16) * mm});
            skLineSegment(sketch, "E90.top", {"start": v(62.47, -107.32) * mm, "end": v(63.74, -107.32) * mm});
            skLineSegment(sketch, "E90.left", {"start": v(62.47, -97.16) * mm, "end": v(62.47, -107.31) * mm});
            skLineSegment(sketch, "E90.right", {"start": v(63.74, -97.16) * mm, "end": v(63.74, -107.31) * mm});
            skLineSegment(sketch, "E91.bottom", {"start": v(131.35, -69.15) * mm, "end": v(132.25, -68.25) * mm});
            skLineSegment(sketch, "E91.top", {"start": v(138.54, -76.33) * mm, "end": v(139.44, -75.43) * mm});
            skLineSegment(sketch, "E91.left", {"start": v(131.35, -69.15) * mm, "end": v(138.54, -76.33) * mm});
            skLineSegment(sketch, "E91.right", {"start": v(132.25, -68.25) * mm, "end": v(139.44, -75.43) * mm});
            skLineSegment(sketch, "E92.bottom", {"start": v(-13.23, 75.43) * mm, "end": v(-12.33, 76.33) * mm});
            skLineSegment(sketch, "E92.top", {"start": v(-11.43, 73.64) * mm, "end": v(-10.54, 74.54) * mm});
            skLineSegment(sketch, "E92.left", {"start": v(-13.23, 75.43) * mm, "end": v(-11.43, 73.64) * mm});
            skLineSegment(sketch, "E92.right", {"start": v(-12.33, 76.33) * mm, "end": v(-10.54, 74.54) * mm});
            skLineSegment(sketch, "E93.bottom", {"start": v(-6.04, -68.25) * mm, "end": v(-5.15, -69.15) * mm});
            skLineSegment(sketch, "E93.top", {"start": v(-13.23, -75.43) * mm, "end": v(-12.33, -76.33) * mm});
            skLineSegment(sketch, "E93.left", {"start": v(-6.04, -68.25) * mm, "end": v(-13.23, -75.43) * mm});
            skLineSegment(sketch, "E93.right", {"start": v(-5.15, -69.15) * mm, "end": v(-12.33, -76.33) * mm});
            skLineSegment(sketch, "E94.bottom", {"start": v(138.54, 76.33) * mm, "end": v(139.44, 75.43) * mm});
            skLineSegment(sketch, "E94.top", {"start": v(131.35, 69.15) * mm, "end": v(132.25, 68.25) * mm});
            skLineSegment(sketch, "E94.left", {"start": v(138.54, 76.33) * mm, "end": v(131.35, 69.15) * mm});
            skLineSegment(sketch, "E94.right", {"start": v(139.44, 75.43) * mm, "end": v(132.25, 68.25) * mm});
            skSolve(sketch);
        }
        {
            var Q0;
            Q0 = qSketchRegion(id + "F42", true);
            extrude(context, id + "F43", {"entities" : qUnion([Q0]), "operationType" : NewBodyOperationType.ADD, "depth" : 1.27 * mm});
        }
        {
            var Q0;
            Q0=makeQuery(id+"F4.opRevolve","SWEPT_FACE",FACE,{"disambiguationData":[OSD([sQuery(id+"F3.wireOp",EDGE,"E12")])]});
            var sketch = newSketch(context, id + "F44", { "sketchPlane" : qUnion([Q0])});
            skLineSegment(sketch, "E95", {"start": v(-17.72, 80.82) * mm, "end": v(7.41, 55.7) * mm});
            skLineSegment(sketch, "E96", {"start": v(63.1, 67.28) * mm, "end": v(63.1, 114.3) * mm});
            skLineSegment(sketch, "E97", {"start": v(143.93, 80.82) * mm, "end": v(121.58, 58.48) * mm});
            skLineSegment(sketch, "E98", {"start": v(123.53, 0) * mm, "end": v(177.4, 0) * mm});
            skLineSegment(sketch, "E99", {"start": v(113.45, -50.35) * mm, "end": v(143.93, -80.82) * mm});
            skLineSegment(sketch, "E100", {"start": v(63.1, -114.3) * mm, "end": v(63.1, -72.28) * mm});
            skLineSegment(sketch, "E101", {"start": v(12.84, -50.27) * mm, "end": v(-17.72, -80.82) * mm});
            skLineSegment(sketch, "E102", {"start": v(2.9, 0) * mm, "end": v(-51.2, 0) * mm});
            skSolve(sketch);
        }
        {
            var Q0;
            Q0=makeQuery(id+"F4.opRevolve","SWEPT_FACE",FACE,{"disambiguationData":[OSD([sQuery(id+"F3.wireOp",EDGE,"E12")])]});
            var sketch = newSketch(context, id + "F45", { "sketchPlane" : qUnion([Q0])});
            skLineSegment(sketch, "E103.bottom", {"start": v(62.47, 114.3) * mm, "end": v(63.74, 114.3) * mm});
            skLineSegment(sketch, "E103.top", {"start": v(62.47, 107.95) * mm, "end": v(63.74, 107.95) * mm});
            skLineSegment(sketch, "E103.left", {"start": v(62.47, 114.3) * mm, "end": v(62.47, 107.95) * mm});
            skLineSegment(sketch, "E103.right", {"start": v(63.74, 114.3) * mm, "end": v(63.74, 107.95) * mm});
            skLineSegment(sketch, "E104.bottom", {"start": v(143.48, 81.27) * mm, "end": v(144.37, 80.37) * mm});
            skLineSegment(sketch, "E104.top", {"start": v(138.99, 76.78) * mm, "end": v(139.88, 75.88) * mm});
            skLineSegment(sketch, "E104.left", {"start": v(143.48, 81.27) * mm, "end": v(138.99, 76.78) * mm});
            skLineSegment(sketch, "E104.right", {"start": v(144.37, 80.37) * mm, "end": v(139.88, 75.88) * mm});
            skLineSegment(sketch, "E105.bottom", {"start": v(171.05, -0.63) * mm, "end": v(171.05, 0.63) * mm});
            skLineSegment(sketch, "E105.top", {"start": v(177.4, -0.63) * mm, "end": v(177.4, 0.63) * mm});
            skLineSegment(sketch, "E105.left", {"start": v(171.05, -0.64) * mm, "end": v(177.4, -0.64) * mm});
            skLineSegment(sketch, "E105.right", {"start": v(171.05, 0.64) * mm, "end": v(177.4, 0.64) * mm});
            skLineSegment(sketch, "E106.bottom", {"start": v(138.99, -76.78) * mm, "end": v(139.88, -75.88) * mm});
            skLineSegment(sketch, "E106.top", {"start": v(143.48, -81.27) * mm, "end": v(144.37, -80.37) * mm});
            skLineSegment(sketch, "E106.left", {"start": v(138.99, -76.78) * mm, "end": v(143.48, -81.27) * mm});
            skLineSegment(sketch, "E106.right", {"start": v(139.88, -75.88) * mm, "end": v(144.37, -80.37) * mm});
            skLineSegment(sketch, "E107.bottom", {"start": v(62.47, -107.95) * mm, "end": v(63.74, -107.95) * mm});
            skLineSegment(sketch, "E107.top", {"start": v(62.47, -114.3) * mm, "end": v(63.74, -114.3) * mm});
            skLineSegment(sketch, "E107.left", {"start": v(62.47, -107.95) * mm, "end": v(62.47, -114.3) * mm});
            skLineSegment(sketch, "E107.right", {"start": v(63.74, -107.95) * mm, "end": v(63.74, -114.3) * mm});
            skLineSegment(sketch, "E108.bottom", {"start": v(-13.68, -75.88) * mm, "end": v(-12.78, -76.78) * mm});
            skLineSegment(sketch, "E108.top", {"start": v(-18.17, -80.37) * mm, "end": v(-17.27, -81.27) * mm});
            skLineSegment(sketch, "E108.left", {"start": v(-13.68, -75.88) * mm, "end": v(-18.17, -80.37) * mm});
            skLineSegment(sketch, "E108.right", {"start": v(-12.78, -76.78) * mm, "end": v(-17.27, -81.27) * mm});
            skLineSegment(sketch, "E109.bottom", {"start": v(-51.2, -0.63) * mm, "end": v(-51.2, 0.63) * mm});
            skLineSegment(sketch, "E109.top", {"start": v(-44.85, -0.63) * mm, "end": v(-44.85, 0.63) * mm});
            skLineSegment(sketch, "E109.left", {"start": v(-51.2, -0.64) * mm, "end": v(-44.85, -0.64) * mm});
            skLineSegment(sketch, "E109.right", {"start": v(-51.2, 0.64) * mm, "end": v(-44.85, 0.64) * mm});
            skLineSegment(sketch, "E110.bottom", {"start": v(-18.17, 80.37) * mm, "end": v(-17.27, 81.27) * mm});
            skLineSegment(sketch, "E110.top", {"start": v(-13.68, 75.88) * mm, "end": v(-12.78, 76.78) * mm});
            skLineSegment(sketch, "E110.left", {"start": v(-18.17, 80.37) * mm, "end": v(-13.68, 75.88) * mm});
            skLineSegment(sketch, "E110.right", {"start": v(-17.27, 81.27) * mm, "end": v(-12.78, 76.78) * mm});
            skSolve(sketch);
        }
        {
            var Q0;
            Q0 = qSketchRegion(id + "F45", true);
            extrude(context, id + "F46", {"entities" : qUnion([Q0]), "operationType" : NewBodyOperationType.ADD, "depth" : 1.27 * mm});
        }
        {
            var Q0;
            Q0=makeQuery(id+"F39.opExtrude","SWEPT_BODY",BODY,{"disambiguationData":[OSD([sQuery(id+"F38.wireOp",EDGE,"E71.bottom"),sQuery(id+"F38.wireOp",EDGE,"E71.top"),sQuery(id+"F38.wireOp",EDGE,"E71.left"),sQuery(id+"F38.wireOp",EDGE,"E71.right")])]});
            var Q1;
            Q1=makeQuery(id+"F4.opRevolve","SWEPT_BODY",BODY,{"disambiguationData":[OSD([sQuery(id+"F3.wireOp",EDGE,"E5"),sQuery(id+"F3.wireOp",EDGE,"E6"),sQuery(id+"F3.wireOp",EDGE,"E7"),sQuery(id+"F3.wireOp",EDGE,"E8"),sQuery(id+"F3.wireOp",EDGE,"E9"),sQuery(id+"F3.wireOp",EDGE,"E10"),sQuery(id+"F3.wireOp",EDGE,"E11"),sQuery(id+"F3.wireOp",EDGE,"E12")])]});
            var Q2;
            Q2=makeQuery(id+"F2.opRevolve","SWEPT_BODY",BODY,{"disambiguationData":[OSD([sQuery(id+"F1.wireOp",EDGE,"E2.bottom"),sQuery(id+"F1.wireOp",EDGE,"E2.top"),sQuery(id+"F1.wireOp",EDGE,"E2.left"),sQuery(id+"F1.wireOp",EDGE,"E2.right"),sQuery(id+"F1.wireOp",EDGE,"E3"),sQuery(id+"F1.wireOp",EDGE,"E4")])]});
            var Q3;
            Q3=qCreatedBy(makeId("Origin.pointOp"),VERTEX);
            transform(context, id + "F47", {"entities" : qUnion([Q0, Q1, Q2]), "transformType" : TransformType.SCALE_UNIFORMLY, "scale" : 0.85, "makeCopy" : true, "scalePoint" : qUnion([Q3])});
        }
        {
            var Q0;
            Q0=qCreatedBy(makeId("Front.planeOp"),FACE);
            var sketch = newSketch(context, id + "F48", { "sketchPlane" : qUnion([Q0])});
            skLineSegment(sketch, "E111.bottom", {"start": v(-20.32, 42.45) * mm, "end": v(-7.62, 42.45) * mm});
            skLineSegment(sketch, "E111.top", {"start": v(-20.32, 40.17) * mm, "end": v(-7.62, 40.17) * mm});
            skLineSegment(sketch, "E111.left", {"start": v(-20.32, 42.45) * mm, "end": v(-20.32, 40.17) * mm});
            skLineSegment(sketch, "E111.right", {"start": v(-7.62, 42.45) * mm, "end": v(-7.62, 40.17) * mm});
            skLineSegment(sketch, "E112", {"start": v(0, 68.57) * mm, "end": v(0, 0) * mm});
            skSolve(sketch);
        }
        {
            var Q0;
            Q0 = qSketchRegion(id + "F48", true);
            var Q1;
            Q1=sQuery(id+"F48.wireOp",EDGE,"E112");
            revolve(context, id + "F49", {"entities" : qUnion([Q0]), "axis" : qUnion([Q1]), "revolveType" : RevolveType.FULL});
        }
        {
            var Q0;
            Q0=makeQuery(id+"F49.opRevolve","SWEPT_BODY",BODY,{"disambiguationData":[OSD([sQuery(id+"F48.wireOp",EDGE,"E111.bottom"),sQuery(id+"F48.wireOp",EDGE,"E111.top"),sQuery(id+"F48.wireOp",EDGE,"E111.left"),sQuery(id+"F48.wireOp",EDGE,"E111.right")])]});
            var Q1;
            Q1=qCreatedBy(makeId("Origin.pointOp"),VERTEX);
            transform(context, id + "F50", {"entities" : qUnion([Q0]), "transformType" : TransformType.SCALE_UNIFORMLY, "scale" : 0.85, "makeCopy" : true, "scalePoint" : qUnion([Q1])});
        }
    });
